SOLIDWORKS PART (.sldprt)
format: sldprt  version: not decoded by parser v0  size: 212,992 bytes
history: native  units: mm
features: sketch x7, extrude x3, chamfer x3, cut_extrude x3, material x1, plane x1 (+13 scaffold rows collapsed)
feature tree (31):
  scaffold x13  (default folders/planes/origin — collapsed)
  material  "Material <not specified>"
  sketch  "Sketch1"  dims[D1=20.0mm D2=30.0mm D3=15.0mm D4=15.0mm D5=3.0mm D6=3.0mm D7=~13.695639mm]
  extrude  "Boss-Extrude1"  Depth=4mm
  sketch  "Sketch2"  dims[D1=2.1mm]
  sketch  "Sketch3"  dims[D1=3.0mm]
  extrude  "Boss-Extrude2"  Depth=30mm
  sketch  "Sketch4"  dims[D1=0.5mm D2=23.0mm]
  extrude  "Boss-Extrude3"  Depth=4mm
  plane  "Plane1"
  chamfer  "Chamfer1"  Distance=5mm Angle=45deg
  chamfer  "Chamfer2"  Distance=5mm Angle=45deg
  chamfer  "Chamfer3"  Distance=1mm Angle=45deg
  sketch  "Sketch6"  dims[c1.D1=3.1mm c1.D2=3.1mm c1.D3=3.1mm c1.D4=3.1mm c2.D1=~6.124961mm c2.D4=~7.000419mm c2.D5=6.0mm c2.D6=13.0mm]
  cut_extrude  "Cut-Extrude3"  [1 undecoded]
  sketch  "Sketch7"  dims[D1=4.8mm]
  cut_extrude  "Cut-Extrude4"  [1 undecoded]
  sketch  "Sketch8"
  cut_extrude  "Cut-Extrude5"  [1 undecoded]
decode coverage: 12 of 16 modeling features carry decoded parameters
note: ~ marks probable driven/reference dimensions
note: 3 parameter values undecoded
summary: no parameter record found for 3 features
note: suppression state not decoded; provenance and decode notes live in map.json
